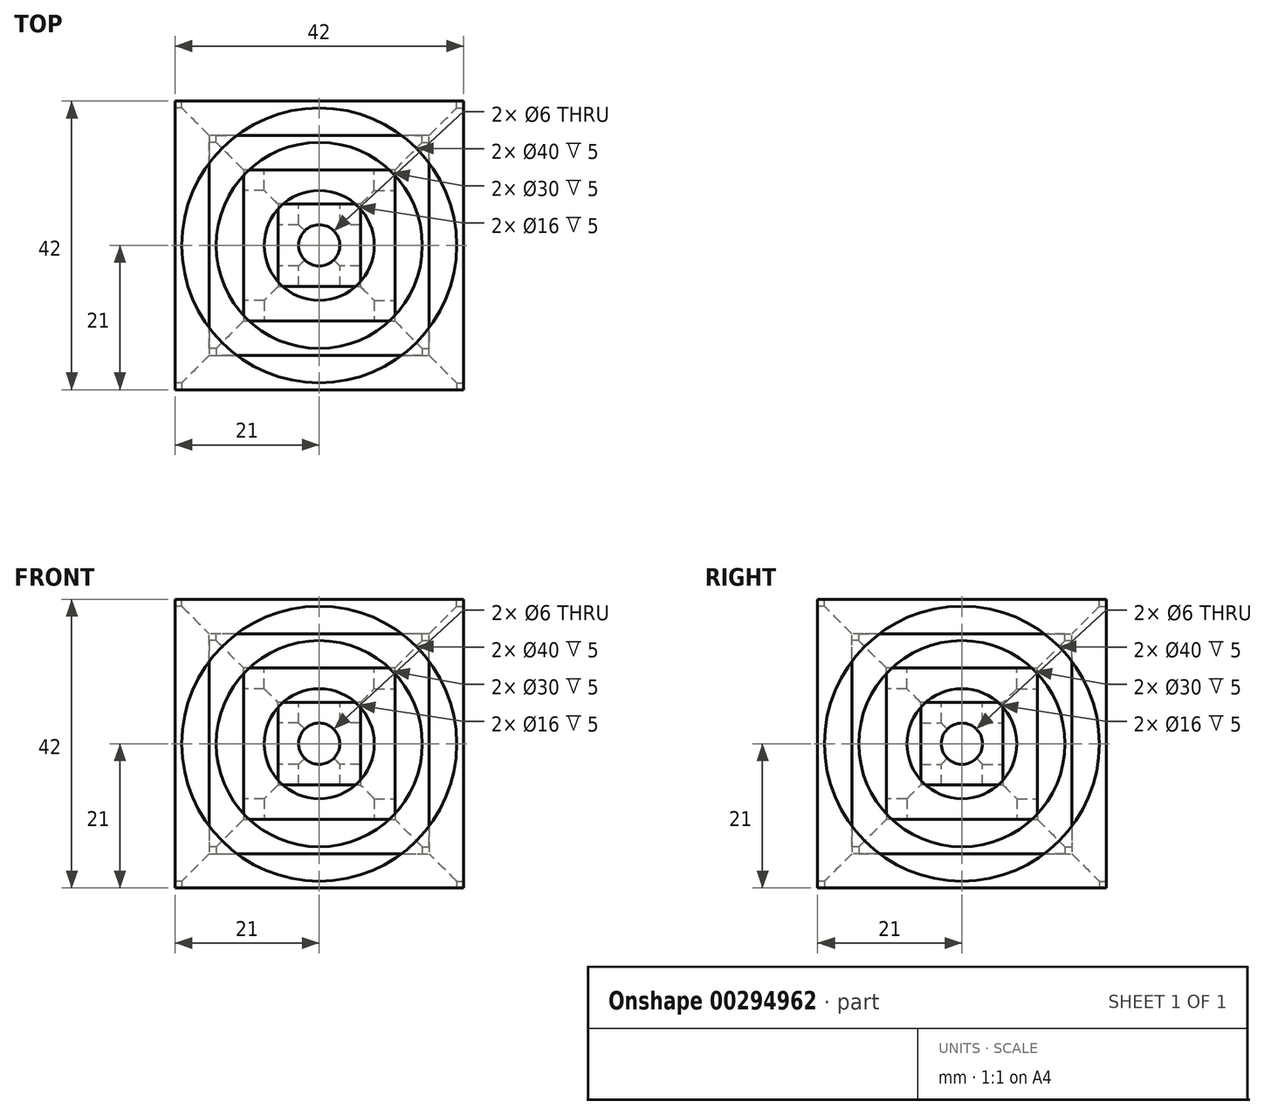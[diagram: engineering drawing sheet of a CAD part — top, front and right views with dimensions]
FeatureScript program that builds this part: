
annotation { "Feature Type Name" : "Feature", "Feature Type Description" : "" }
export const myFeature = defineFeature(function(context is Context, id is Id, definition is map)
    precondition{}
    {
        {
            var Q0;
            Q0=qCreatedBy(makeId("Front.planeOp"),FACE);
            var sketch = newSketch(context, id + "F0", { "sketchPlane" : qUnion([Q0])});
            skLineSegment(sketch, "E0.bottom", {"start": v(-21, 21) * mm, "end": v(21, 21) * mm});
            skLineSegment(sketch, "E0.top", {"start": v(-21, -21) * mm, "end": v(21, -21) * mm});
            skLineSegment(sketch, "E0.left", {"start": v(-21, 21) * mm, "end": v(-21, -21) * mm});
            skLineSegment(sketch, "E0.right", {"start": v(21, 21) * mm, "end": v(21, -21) * mm});
            skPoint(sketch, "E0.middle", {"position": v(0, 0) * mm});
            skCircle(sketch, "E1", {"center": v(0, 0) * mm, "radius": 3 * mm});
            skSolve(sketch);
        }
        {
            var Q0;
            Q0=makeQuery(id+"F0.imprint","IMPRINT",FACE,{"disambiguationData":[TD([[makeQuery(id+"F0.imprint","IMPRINT",EDGE,{"derivedFrom":sQuery(id+"F0.wireOp",EDGE,"E0.bottom")}),-1.0]])]});
            extrude(context, id + "F1", {"entities" : qUnion([Q0]), "depth" : 42 * mm});
        }
        {
            var Q0;
            Q0=makeQuery(id+"F1.opExtrude","CAP_FACE",FACE,{"disambiguationData":[OSD([sQuery(id+"F0.wireOp",EDGE,"E0.bottom"),sQuery(id+"F0.wireOp",EDGE,"E0.top"),sQuery(id+"F0.wireOp",EDGE,"E0.left"),sQuery(id+"F0.wireOp",EDGE,"E0.right"),sQuery(id+"F0.wireOp",EDGE,"E1")])],"isStart":false});
            var sketch = newSketch(context, id + "F2", { "sketchPlane" : qUnion([Q0])});
            skCircle(sketch, "E2", {"center": v(0, 0) * mm, "radius": 20 * mm});
            skCircle(sketch, "E3", {"center": v(0, 0) * mm, "radius": 8 * mm});
            skCircle(sketch, "E4", {"center": v(0, 0) * mm, "radius": 15 * mm});
            skSolve(sketch);
        }
        {
            var Q0;
            Q0=makeQuery(id+"F2.imprint","IMPRINT",FACE,{"disambiguationData":[TD([[makeQuery(id+"F2.imprint","IMPRINT",EDGE,{"derivedFrom":sQuery(id+"F2.wireOp",EDGE,"E2")}),1.0]])]});
            extrude(context, id + "F3", {"entities" : qUnion([Q0]), "operationType" : NewBodyOperationType.REMOVE, "oppositeDirection" : true, "depth" : 5 * mm});
        }
        {
            var Q0;
            Q0=makeQuery(id+"F2.imprint","IMPRINT",FACE,{"disambiguationData":[TD([[makeQuery(id+"F2.imprint","IMPRINT",EDGE,{"derivedFrom":sQuery(id+"F2.wireOp",EDGE,"E3")}),-1.0]])]});
            extrude(context, id + "F4", {"entities" : qUnion([Q0]), "operationType" : NewBodyOperationType.REMOVE, "oppositeDirection" : true, "depth" : 10 * mm});
        }
        {
            var Q0;
            Q0=makeQuery(id+"F2.imprint","IMPRINT",FACE,{"disambiguationData":[TD([[makeQuery(id+"F2.imprint","IMPRINT",EDGE,{"derivedFrom":sQuery(id+"F2.wireOp",EDGE,"E3")}),1.0]])]});
            extrude(context, id + "F5", {"entities" : qUnion([Q0]), "operationType" : NewBodyOperationType.REMOVE, "oppositeDirection" : true, "depth" : 15 * mm});
        }
        {
            var Q0;
            Q0=makeQuery(id+"F1.opExtrude","SWEPT_FACE",FACE,{"disambiguationData":[OSD([sQuery(id+"F0.wireOp",EDGE,"E0.left")])]});
            var sketch = newSketch(context, id + "F6", { "sketchPlane" : qUnion([Q0])});
            skCircle(sketch, "E5", {"center": v(21, 0) * mm, "radius": 3 * mm});
            skPoint(sketch, "E5.centerSnap0", {"position": v(21, 21) * mm});
            skCircle(sketch, "E6", {"center": v(21, 0) * mm, "radius": 8 * mm});
            skCircle(sketch, "E7", {"center": v(21, 0) * mm, "radius": 15 * mm});
            skCircle(sketch, "E8", {"center": v(21, 0) * mm, "radius": 20 * mm});
            skSolve(sketch);
        }
        {
            var Q0;
            Q0=makeQuery(id+"F6.imprint","IMPRINT",FACE,{"disambiguationData":[TD([[makeQuery(id+"F6.imprint","IMPRINT",EDGE,{"derivedFrom":sQuery(id+"F6.wireOp",EDGE,"E7")}),-1.0]])]});
            extrude(context, id + "F7", {"entities" : qUnion([Q0]), "operationType" : NewBodyOperationType.REMOVE, "oppositeDirection" : true, "depth" : 5 * mm});
        }
        {
            var Q0;
            Q0=makeQuery(id+"F6.imprint","IMPRINT",FACE,{"disambiguationData":[TD([[makeQuery(id+"F6.imprint","IMPRINT",EDGE,{"derivedFrom":sQuery(id+"F6.wireOp",EDGE,"E6")}),-1.0]])]});
            extrude(context, id + "F8", {"entities" : qUnion([Q0]), "operationType" : NewBodyOperationType.REMOVE, "oppositeDirection" : true, "depth" : 10 * mm});
        }
        {
            var Q0;
            Q0=makeQuery(id+"F6.imprint","IMPRINT",FACE,{"disambiguationData":[TD([[makeQuery(id+"F6.imprint","IMPRINT",EDGE,{"derivedFrom":sQuery(id+"F6.wireOp",EDGE,"E5")}),-1.0]])]});
            extrude(context, id + "F9", {"entities" : qUnion([Q0]), "operationType" : NewBodyOperationType.REMOVE, "oppositeDirection" : true, "depth" : 15 * mm});
        }
        {
            var Q0;
            Q0=makeQuery(id+"F6.imprint","IMPRINT",FACE,{"disambiguationData":[TD([[makeQuery(id+"F6.imprint","IMPRINT",EDGE,{"derivedFrom":sQuery(id+"F6.wireOp",EDGE,"E5")}),1.0]])]});
            extrude(context, id + "F10", {"entities" : qUnion([Q0]), "operationType" : NewBodyOperationType.REMOVE, "oppositeDirection" : true, "depth" : 42 * mm});
        }
        {
            var Q0;
            Q0=makeQuery(id+"F1.opExtrude","CAP_FACE",FACE,{"disambiguationData":[OSD([sQuery(id+"F0.wireOp",EDGE,"E0.bottom"),sQuery(id+"F0.wireOp",EDGE,"E0.top"),sQuery(id+"F0.wireOp",EDGE,"E0.left"),sQuery(id+"F0.wireOp",EDGE,"E0.right"),sQuery(id+"F0.wireOp",EDGE,"E1")])],"isStart":true});
            var sketch = newSketch(context, id + "F11", { "sketchPlane" : qUnion([Q0])});
            skCircle(sketch, "E9", {"center": v(0, 0) * mm, "radius": 3 * mm});
            skCircle(sketch, "E10", {"center": v(0, 0) * mm, "radius": 8 * mm});
            skCircle(sketch, "E11", {"center": v(0, 0) * mm, "radius": 15 * mm});
            skCircle(sketch, "E12", {"center": v(0, 0) * mm, "radius": 20 * mm});
            skSolve(sketch);
        }
        {
            var Q0;
            Q0=makeQuery(id+"F11.imprint","IMPRINT",FACE,{"disambiguationData":[TD([[makeQuery(id+"F11.imprint","IMPRINT",EDGE,{"derivedFrom":sQuery(id+"F11.wireOp",EDGE,"E11")}),-1.0]])]});
            extrude(context, id + "F12", {"entities" : qUnion([Q0]), "operationType" : NewBodyOperationType.REMOVE, "oppositeDirection" : true, "depth" : 5 * mm});
        }
        {
            var Q0;
            Q0=makeQuery(id+"F11.imprint","IMPRINT",FACE,{"disambiguationData":[TD([[makeQuery(id+"F11.imprint","IMPRINT",EDGE,{"derivedFrom":sQuery(id+"F11.wireOp",EDGE,"E10")}),-1.0]])]});
            extrude(context, id + "F13", {"entities" : qUnion([Q0]), "operationType" : NewBodyOperationType.REMOVE, "oppositeDirection" : true, "depth" : 10 * mm});
        }
        {
            var Q0;
            Q0=makeQuery(id+"F11.imprint","IMPRINT",FACE,{"disambiguationData":[TD([[makeQuery(id+"F11.imprint","IMPRINT",EDGE,{"derivedFrom":sQuery(id+"F11.wireOp",EDGE,"E9")}),1.0]])]});
            extrude(context, id + "F14", {"entities" : qUnion([Q0]), "operationType" : NewBodyOperationType.REMOVE, "oppositeDirection" : true, "depth" : 15 * mm});
        }
        {
            var Q0;
            Q0=makeQuery(id+"F1.opExtrude","SWEPT_FACE",FACE,{"disambiguationData":[OSD([sQuery(id+"F0.wireOp",EDGE,"E0.right")])]});
            var sketch = newSketch(context, id + "F15", { "sketchPlane" : qUnion([Q0])});
            skCircle(sketch, "E13", {"center": v(-21, 0) * mm, "radius": 3 * mm});
            skCircle(sketch, "E14", {"center": v(-21, 0) * mm, "radius": 8 * mm});
            skCircle(sketch, "E15", {"center": v(-21, 0) * mm, "radius": 15 * mm});
            skCircle(sketch, "E16", {"center": v(-21, 0) * mm, "radius": 20 * mm});
            skSolve(sketch);
        }
        {
            var Q0;
            Q0=makeQuery(id+"F15.imprint","IMPRINT",FACE,{"disambiguationData":[TD([[makeQuery(id+"F15.imprint","IMPRINT",EDGE,{"derivedFrom":sQuery(id+"F15.wireOp",EDGE,"E15")}),-1.0]])]});
            extrude(context, id + "F16", {"entities" : qUnion([Q0]), "operationType" : NewBodyOperationType.REMOVE, "oppositeDirection" : true, "depth" : 5 * mm});
        }
        {
            var Q0;
            Q0=makeQuery(id+"F15.imprint","IMPRINT",FACE,{"disambiguationData":[TD([[makeQuery(id+"F15.imprint","IMPRINT",EDGE,{"derivedFrom":sQuery(id+"F15.wireOp",EDGE,"E14")}),-1.0]])]});
            extrude(context, id + "F17", {"entities" : qUnion([Q0]), "operationType" : NewBodyOperationType.REMOVE, "oppositeDirection" : true, "depth" : 10 * mm});
        }
        {
            var Q0;
            Q0=makeQuery(id+"F15.imprint","IMPRINT",FACE,{"disambiguationData":[TD([[makeQuery(id+"F15.imprint","IMPRINT",EDGE,{"derivedFrom":sQuery(id+"F15.wireOp",EDGE,"E13")}),1.0]])]});
            extrude(context, id + "F18", {"entities" : qUnion([Q0]), "operationType" : NewBodyOperationType.REMOVE, "oppositeDirection" : true, "depth" : 15 * mm});
        }
        {
            var Q0;
            Q0=makeQuery(id+"F1.opExtrude","SWEPT_FACE",FACE,{"disambiguationData":[OSD([sQuery(id+"F0.wireOp",EDGE,"E0.bottom")])]});
            var sketch = newSketch(context, id + "F19", { "sketchPlane" : qUnion([Q0])});
            skCircle(sketch, "E17", {"center": v(0, -21) * mm, "radius": 3 * mm});
            skPoint(sketch, "E17.centerSnap0", {"position": v(-21, -21) * mm});
            skCircle(sketch, "E18", {"center": v(0, -21) * mm, "radius": 8 * mm});
            skCircle(sketch, "E19", {"center": v(0, -21) * mm, "radius": 15 * mm});
            skCircle(sketch, "E20", {"center": v(0, -21) * mm, "radius": 20 * mm});
            skSolve(sketch);
        }
        {
            var Q0;
            Q0=makeQuery(id+"F19.imprint","IMPRINT",FACE,{"disambiguationData":[TD([[makeQuery(id+"F19.imprint","IMPRINT",EDGE,{"derivedFrom":sQuery(id+"F19.wireOp",EDGE,"E19")}),-1.0]])]});
            extrude(context, id + "F20", {"entities" : qUnion([Q0]), "operationType" : NewBodyOperationType.REMOVE, "oppositeDirection" : true, "depth" : 5 * mm});
        }
        {
            var Q0;
            Q0=makeQuery(id+"F19.imprint","IMPRINT",FACE,{"disambiguationData":[TD([[makeQuery(id+"F19.imprint","IMPRINT",EDGE,{"derivedFrom":sQuery(id+"F19.wireOp",EDGE,"E18")}),-1.0]])]});
            extrude(context, id + "F21", {"entities" : qUnion([Q0]), "operationType" : NewBodyOperationType.REMOVE, "oppositeDirection" : true, "depth" : 10 * mm});
        }
        {
            var Q0;
            Q0=makeQuery(id+"F19.imprint","IMPRINT",FACE,{"disambiguationData":[TD([[makeQuery(id+"F19.imprint","IMPRINT",EDGE,{"derivedFrom":sQuery(id+"F19.wireOp",EDGE,"E17")}),-1.0]])]});
            extrude(context, id + "F22", {"entities" : qUnion([Q0]), "operationType" : NewBodyOperationType.REMOVE, "oppositeDirection" : true, "depth" : 15 * mm});
        }
        {
            var Q0;
            Q0=makeQuery(id+"F19.imprint","IMPRINT",FACE,{"disambiguationData":[TD([[makeQuery(id+"F19.imprint","IMPRINT",EDGE,{"derivedFrom":sQuery(id+"F19.wireOp",EDGE,"E17")}),1.0]])]});
            extrude(context, id + "F23", {"entities" : qUnion([Q0]), "operationType" : NewBodyOperationType.REMOVE, "oppositeDirection" : true, "depth" : 42 * mm});
        }
        {
            var Q0;
            Q0=makeQuery(id+"F1.opExtrude","SWEPT_FACE",FACE,{"disambiguationData":[OSD([sQuery(id+"F0.wireOp",EDGE,"E0.top")])]});
            var sketch = newSketch(context, id + "F24", { "sketchPlane" : qUnion([Q0])});
            skCircle(sketch, "E21", {"center": v(0, 21) * mm, "radius": 3 * mm});
            skCircle(sketch, "E22", {"center": v(0, 21) * mm, "radius": 8 * mm});
            skCircle(sketch, "E23", {"center": v(0, 21) * mm, "radius": 15 * mm});
            skCircle(sketch, "E24", {"center": v(0, 21) * mm, "radius": 20 * mm});
            skSolve(sketch);
        }
        {
            var Q0;
            Q0=makeQuery(id+"F24.imprint","IMPRINT",FACE,{"disambiguationData":[TD([[makeQuery(id+"F24.imprint","IMPRINT",EDGE,{"derivedFrom":sQuery(id+"F24.wireOp",EDGE,"E23")}),-1.0]])]});
            extrude(context, id + "F25", {"entities" : qUnion([Q0]), "operationType" : NewBodyOperationType.REMOVE, "oppositeDirection" : true, "depth" : 5 * mm});
        }
        {
            var Q0;
            Q0=makeQuery(id+"F24.imprint","IMPRINT",FACE,{"disambiguationData":[TD([[makeQuery(id+"F24.imprint","IMPRINT",EDGE,{"derivedFrom":sQuery(id+"F24.wireOp",EDGE,"E22")}),-1.0]])]});
            extrude(context, id + "F26", {"entities" : qUnion([Q0]), "operationType" : NewBodyOperationType.REMOVE, "oppositeDirection" : true, "depth" : 10 * mm});
        }
        {
            var Q0;
            Q0=makeQuery(id+"F24.imprint","IMPRINT",FACE,{"disambiguationData":[TD([[makeQuery(id+"F24.imprint","IMPRINT",EDGE,{"derivedFrom":sQuery(id+"F24.wireOp",EDGE,"E21")}),1.0]])]});
            extrude(context, id + "F27", {"entities" : qUnion([Q0]), "operationType" : NewBodyOperationType.REMOVE, "oppositeDirection" : true, "depth" : 15 * mm});
        }
    });
